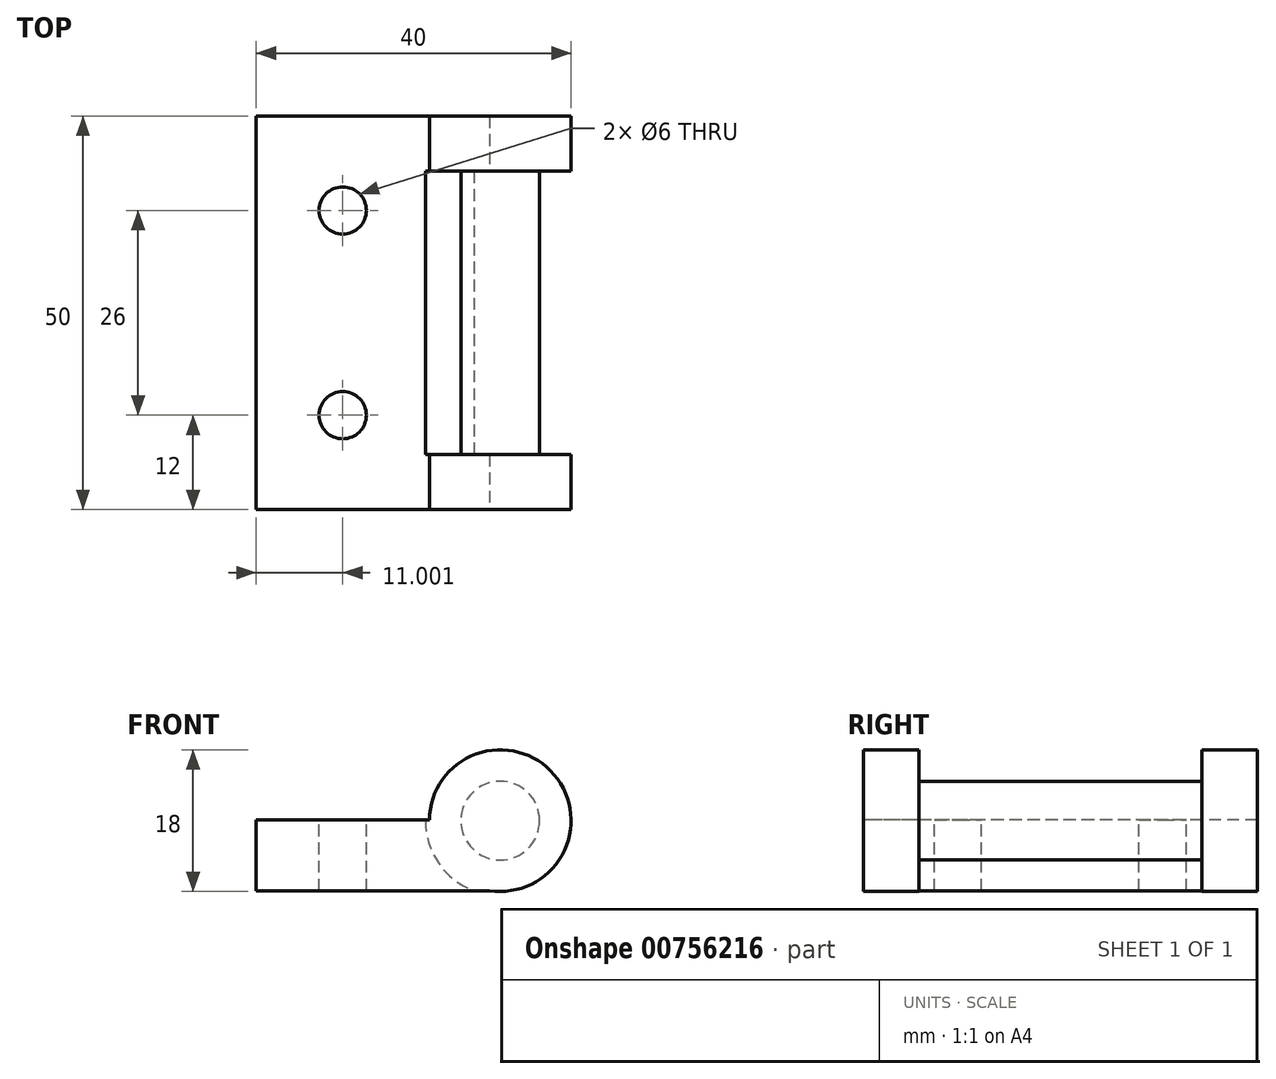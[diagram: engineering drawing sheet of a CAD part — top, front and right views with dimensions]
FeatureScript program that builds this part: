
annotation { "Feature Type Name" : "Feature", "Feature Type Description" : "" }
export const myFeature = defineFeature(function(context is Context, id is Id, definition is map)
    precondition{}
    {
        {
            var Q0;
            Q0=qCreatedBy(makeId("Front.planeOp"),FACE);
            var sketch = newSketch(context, id + "F0", { "sketchPlane" : qUnion([Q0])});
            skLineSegment(sketch, "E0", {"start": v(0, 0) * mm, "end": v(32.37, 0) * mm});
            skLineSegment(sketch, "E1", {"start": v(40, 8.8) * mm, "end": v(40, 9) * mm});
            skLineSegment(sketch, "E2", {"start": v(22, 9) * mm, "end": v(0, 9) * mm});
            skLineSegment(sketch, "E3", {"start": v(0, 9) * mm, "end": v(0, 0) * mm});
            skCircle(sketch, "E4", {"center": v(31, 8.9) * mm, "radius": 9 * mm});
            skPoint(sketch, "E4.second.point", {"position": v(29.64, 0) * mm});
            skPoint(sketch, "E4.third.point", {"position": v(22, 9) * mm});
            skLineSegment(sketch, "E5", {"start": v(0, -10.71) * mm, "end": v(40, -10.71) * mm, "construction": true});
            skLineSegment(sketch, "E6", {"start": v(40, -10.71) * mm, "end": v(40, 9) * mm, "construction": true});
            skLineSegment(sketch, "E7", {"start": v(0, -10.71) * mm, "end": v(0, 0) * mm, "construction": true});
            skSolve(sketch);
        }
        {
            var Q0;
            Q0 = qSketchRegion(id + "F0", true);
            extrude(context, id + "F1", {"entities" : qUnion([Q0]), "oppositeDirection" : true, "depth" : 50 * mm, "offsetDistance" : 25 * mm});
        }
        {
            var Q0;
            Q0=makeQuery(id+"F1.opExtrude","SWEPT_FACE",FACE,{"disambiguationData":[OSD([sQuery(id+"F0.wireOp",EDGE,"E2")])]});
            var sketch = newSketch(context, id + "F2", { "sketchPlane" : qUnion([Q0])});
            skCircle(sketch, "E8", {"center": v(11, 38) * mm, "radius": 3 * mm});
            skPoint(sketch, "E8.centerSnap0", {"position": v(11, 50) * mm});
            skCircle(sketch, "E9", {"center": v(11, 12) * mm, "radius": 3 * mm});
            skSolve(sketch);
        }
        {
            var Q0;
            Q0 = qSketchRegion(id + "F2", true);
            extrude(context, id + "F3", {"entities" : qUnion([Q0]), "operationType" : NewBodyOperationType.REMOVE, "oppositeDirection" : true, "depth" : 25 * mm, "offsetDistance" : 25 * mm});
        }
        {
            var Q0;
            Q0=makeQuery(id+"F1.opExtrude","CAP_FACE",FACE,{"disambiguationData":[OSD([sQuery(id+"F0.wireOp",EDGE,"E0"),sQuery(id+"F0.wireOp",EDGE,"E2"),sQuery(id+"F0.wireOp",EDGE,"E3"),sQuery(id+"F0.wireOp",EDGE,"E4")])],"isStart":true});
            cPlane(context, id + "F4", {"entities" : qUnion([Q0]), "cplaneType" : CPlaneType.OFFSET, "offset" : 7 * mm, "oppositeDirection" : true, "width" : 150 * mm, "height" : 150 * mm});
        }
        {
            var Q0;
            Q0=qCreatedBy(id+"F4.planeOp",FACE);
            var sketch = newSketch(context, id + "F5", { "sketchPlane" : qUnion([Q0])});
            skArc(sketch, "E10.0", {"start": v(29.64, 0) * mm, "mid": v(37.86, 14.72) * mm, "end": v(22, 9) * mm});
            skCircle(sketch, "E11", {"center": v(31, 8.9) * mm, "radius": 9.5 * mm});
            skCircle(sketch, "E12", {"center": v(31, 8.9) * mm, "radius": 5 * mm});
            skSolve(sketch);
        }
        {
            var Q0;
            Q0 = qSketchRegion(id + "F5", true);
            extrude(context, id + "F6", {"entities" : qUnion([Q0]), "operationType" : NewBodyOperationType.REMOVE, "oppositeDirection" : true, "depth" : 36 * mm, "offsetDistance" : 25 * mm});
        }
    });
